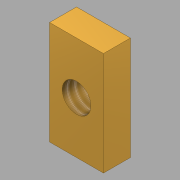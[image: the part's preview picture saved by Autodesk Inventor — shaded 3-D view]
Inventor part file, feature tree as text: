
AUTODESK INVENTOR PART (.ipt)
format: ipt  version: 2020 (Build 240168000, 168)  size: 94,720 bytes
history: native  units: in
note: dims shown in document units (in); Inventor stores cm internally (conversion verified against a paired STEP export)
features: sketch x2, other x1, extrude x1, hole x1
ambient origin geometry x8: Origin, YZ Plane, XZ Plane, XY Plane, X Axis, Y Axis, Z Axis, Center Point
bodies: Body1 (feature_tree)
feature tree (5):
  other  "Sólido1"
  extrude  "Extrusión1"  Depth=0.2403in
  hole  "Agujero1"  [1 undecoded]
  sketch  "Boceto1"  dims[d0=0.125in d1=0.2403in]
  sketch  "Boceto2"  dims[d2=0.0625in d3=0.0in d4=0.2403in d5=0.125in d6=0.0625in d7=0.1201in d8=0.0667in d9=0.172in d10=0.26in d11=0.25in d12=0.5635in d13=0.261in d14=0.8108in]
note: 1 required parameter value undecoded (feature->parameter linkage not recoverable at this tier; creation-order binding heuristic only, values carry confidence <= 0.55)
